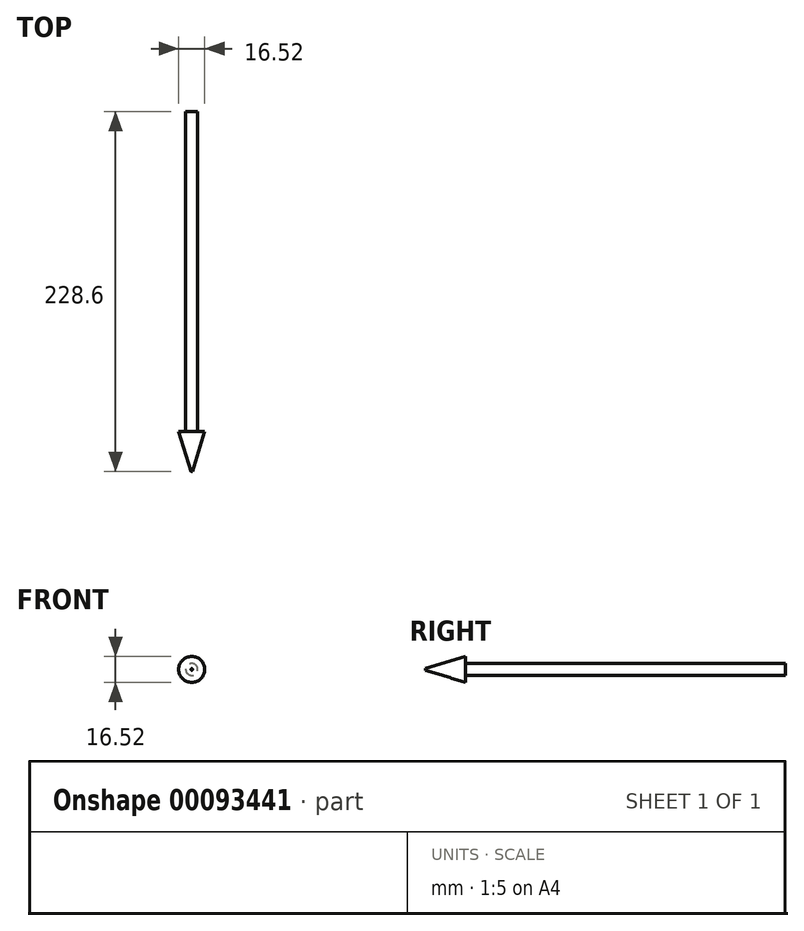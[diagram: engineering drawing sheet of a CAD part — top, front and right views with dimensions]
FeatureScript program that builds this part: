
annotation { "Feature Type Name" : "Feature", "Feature Type Description" : "" }
export const myFeature = defineFeature(function(context is Context, id is Id, definition is map)
    precondition{}
    {
        {
            var Q0;
            Q0=qCreatedBy(makeId("Front.planeOp"),FACE);
            var sketch = newSketch(context, id + "F0", { "sketchPlane" : qUnion([Q0])});
            skCircle(sketch, "E0", {"center": v(0, 0) * mm, "radius": 3.81 * mm});
            skSolve(sketch);
        }
        {
            var Q0;
            Q0 = qSketchRegion(id + "F0", true);
            extrude(context, id + "F1", {"entities" : qUnion([Q0]), "depth" : 203.2 * mm});
        }
        {
            var Q0;
            Q0=makeQuery(id+"F1.opExtrude","CAP_FACE",FACE,{"disambiguationData":[OSD([sQuery(id+"F0.wireOp",EDGE,"E0")])],"isStart":false});
            var sketch = newSketch(context, id + "F2", { "sketchPlane" : qUnion([Q0])});
            skCircle(sketch, "E1", {"center": v(0, 0) * mm, "radius": 8.26 * mm});
            skSolve(sketch);
        }
        {
            var Q0;
            Q0 = qSketchRegion(id + "F2", true);
            extrude(context, id + "F3", {"entities" : qUnion([Q0]), "operationType" : NewBodyOperationType.ADD, "depth" : 25.4 * mm, "hasDraft" : true, "draftAngle" : 17 * degree, "draftPullDirection" : true});
        }
    });
